# Revit family: Lighting_Outside_Nordlux_Arki-100-Outdoor-Garden
name_source: partatom
category: Lighting Fixtures
revit_build: Autodesk Revit 2018 (Build: 20190510_1515(x64)
units: mm (PartAtom-declared; Revit-internal decimal feet)

## family parameters
Always vertical = No
Cut with Voids When Loaded = No
Light Source = Yes
OmniClass Number = 23.35.47.11
OmniClass Title = Lighting Fixtures
Part Type = Normal
Room Calculation Point = No
Round Connector Dimension = Use Diameter
Shared = No
Work Plane-Based = Yes

## types (2) — shared parameters
Apparent Load = 7 VA
Beam angle = 123.70°
CQS = 80.4
CRI / Ra = 79.8
Color Filter = 16777215
Default Elevation = 1219.2 mm  [stored 4 ft]
Description = The Arki series by Danish designer Bønnelycke MDD is characterised by its beautiful dome-like shade and minimalist, clean lines inspired by the classic architect lamp. Arki beautifully balances simplicity with sophistication while emitting the perfect light for your entrance, driveway, terrace or other outdoor space.
Dimming Lamp Color Temperature Shift = <None>
Emit Shape Visible in Rendering = No
Emit from Circle Diameter = 60 mm  [stored 0.19685 ft]
Flicker frequency = 99 Hz
Lens material = Nordlux - Glass - Glass transparent
Manufacturer = Nordlux
Model = Arki 100
NominalVoltage = 230 V
Peak [cd] = 91.7
Photometric Web File = Arki 100 Outdoor Garden Bl..ies
Power factor = 0.53
Product Guid = 0a24aeef-32ba-44fe-8ebd-e91be7998726
Product data url = https://bimobject.com
TM30 Rf = 84.2
TM30 Rg = 93.4
Tilt Angle = 90.00°
URL = www.nordlux.com

## per-type parameters (varying)
| type | Body material | EANNumber |
| ART - (2118108031) - Finish colour - (Galvanized) | Nordlux - Metal - Galvanized steel | 2118108031 |
| ART - (2118108003) - Finish colour - (Black) | Nordlux - Metal - Black | 2118108003 |

note: [stored X ft] marks values corroborated as IEEE doubles in the binary element streams (Revit-internal decimal feet)

## geometry (parser evidence)
native form markers: Sweep x2
no freeform markers — native parametric forms only
